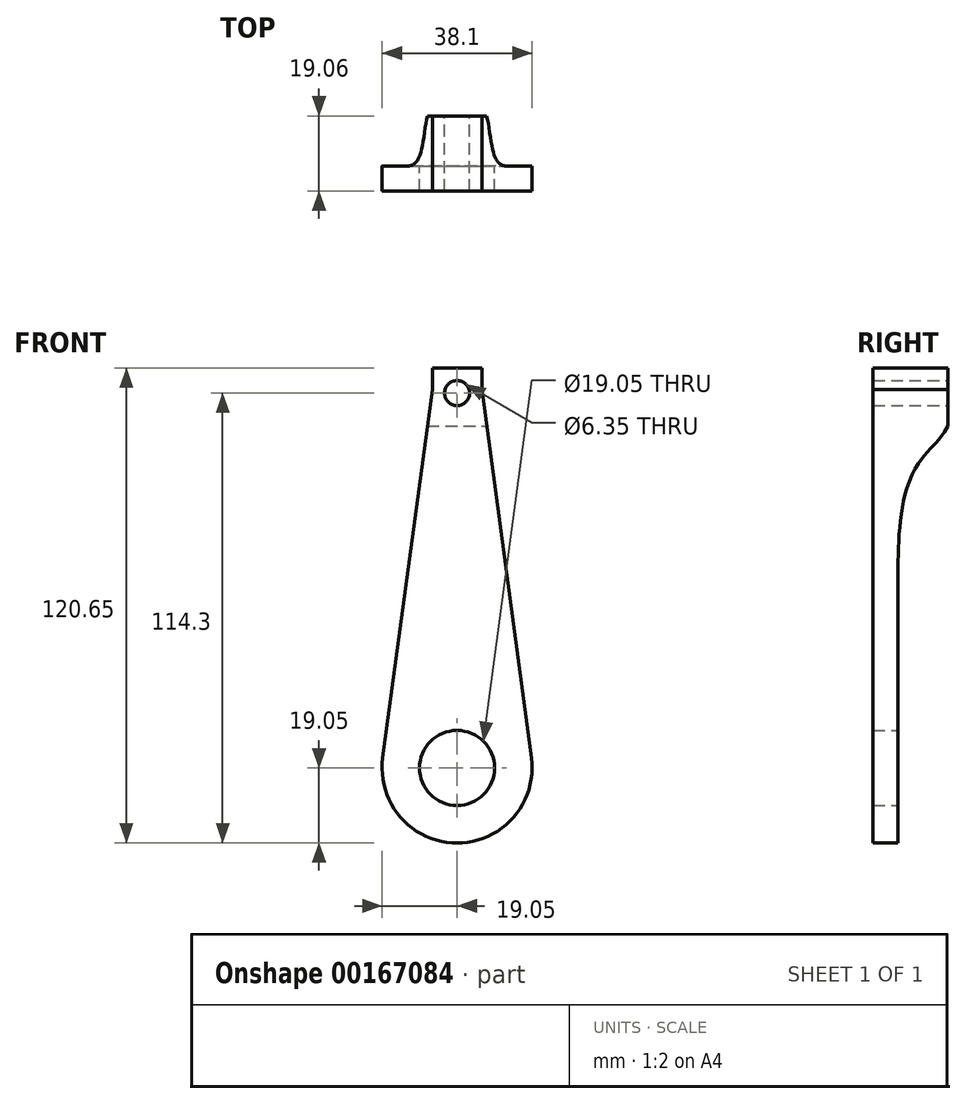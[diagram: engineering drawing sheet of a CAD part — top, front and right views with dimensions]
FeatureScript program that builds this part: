
annotation { "Feature Type Name" : "Feature", "Feature Type Description" : "" }
export const myFeature = defineFeature(function(context is Context, id is Id, definition is map)
    precondition{}
    {
        {
            var Q0;
            Q0=qCreatedBy(makeId("Front.planeOp"),FACE);
            var sketch = newSketch(context, id + "F0", { "sketchPlane" : qUnion([Q0])});
            skCircle(sketch, "E0", {"center": v(0, 0) * mm, "radius": 9.53 * mm});
            skArc(sketch, "E1", {"start": v(-18.88, 2.54) * mm, "mid": v(0, -19.05) * mm, "end": v(18.88, 2.54) * mm});
            skCircle(sketch, "E2", {"center": v(0, 95.25) * mm, "radius": 3.18 * mm});
            skLineSegment(sketch, "E3", {"start": v(-6.3, 96.1) * mm, "end": v(-18.88, 2.54) * mm});
            skLineSegment(sketch, "E4", {"start": v(6.3, 96.1) * mm, "end": v(18.88, 2.54) * mm});
            skLineSegment(sketch, "E5", {"start": v(-6.3, 96.1) * mm, "end": v(-6.3, 101.6) * mm});
            skPoint(sketch, "E5.endSnap0", {"position": v(0, 101.6) * mm});
            skLineSegment(sketch, "E6", {"start": v(-6.3, 101.6) * mm, "end": v(6.3, 101.6) * mm});
            skLineSegment(sketch, "E7", {"start": v(6.3, 101.6) * mm, "end": v(6.3, 96.1) * mm});
            skSolve(sketch);
        }
        {
            var Q0;
            Q0=makeQuery(id+"F0.imprint","IMPRINT",FACE,{"disambiguationData":[TD([[makeQuery(id+"F0.imprint","IMPRINT",EDGE,{"derivedFrom":sQuery(id+"F0.wireOp",EDGE,"E0")}),-1.0]])]});
            extrude(context, id + "F1", {"entities" : qUnion([Q0]), "endBound" : BoundingType.SYMMETRIC, "depth" : 19.05 * mm});
        }
        {
            var Q0;
            Q0=qCreatedBy(makeId("Right.planeOp"),FACE);
            var sketch = newSketch(context, id + "F2", { "sketchPlane" : qUnion([Q0])});
            skLineSegment(sketch, "E8", {"start": v(-3.17, 50.8) * mm, "end": v(12.06, 50.8) * mm});
            skLineSegment(sketch, "E9", {"start": v(12.07, 50.8) * mm, "end": v(12.07, 101.6) * mm});
            skFitSpline(sketch, "E10", {"points": [v(-3.18, 50.8) * mm, v(12.07, 101.6) * mm], "startDerivative": vector(0, 119.67) * mm, "endDerivative": vector(0, 85.93) * mm});
            skLineSegment(sketch, "E11", {"start": v(0, 0) * mm, "end": v(-3.18, 0) * mm});
            skLineSegment(sketch, "E12", {"start": v(-3.18, 0) * mm, "end": v(-3.18, 50.8) * mm});
            skLineSegment(sketch, "E13", {"start": v(-3.18, 0) * mm, "end": v(-3.18, -21.79) * mm});
            skLineSegment(sketch, "E14", {"start": v(-3.18, -21.79) * mm, "end": v(12.06, -21.79) * mm});
            skLineSegment(sketch, "E15", {"start": v(12.06, -21.79) * mm, "end": v(12.07, 50.8) * mm});
            skSolve(sketch);
        }
        {
            var Q0;
            Q0=makeQuery(id+"F2.imprint","IMPRINT",FACE,{"disambiguationData":[TD([[makeQuery(id+"F2.imprint","IMPRINT",EDGE,{"derivedFrom":sQuery(id+"F2.wireOp",EDGE,"E8")}),1.0]])]});
            var Q1;
            Q1=makeQuery(id+"F2.imprint","IMPRINT",FACE,{"disambiguationData":[TD([[makeQuery(id+"F2.imprint","IMPRINT",EDGE,{"derivedFrom":sQuery(id+"F2.wireOp",EDGE,"E8")}),-1.0]])]});
            extrude(context, id + "F3", {"entities" : qUnion([Q0, Q1]), "operationType" : NewBodyOperationType.REMOVE, "endBound" : BoundingType.THROUGH_ALL, "oppositeDirection" : true, "depth" : 25.4 * mm, "hasSecondDirection" : true, "secondDirectionOppositeDirection" : false, "secondDirectionDepth" : 25.4 * mm});
        }
    });
